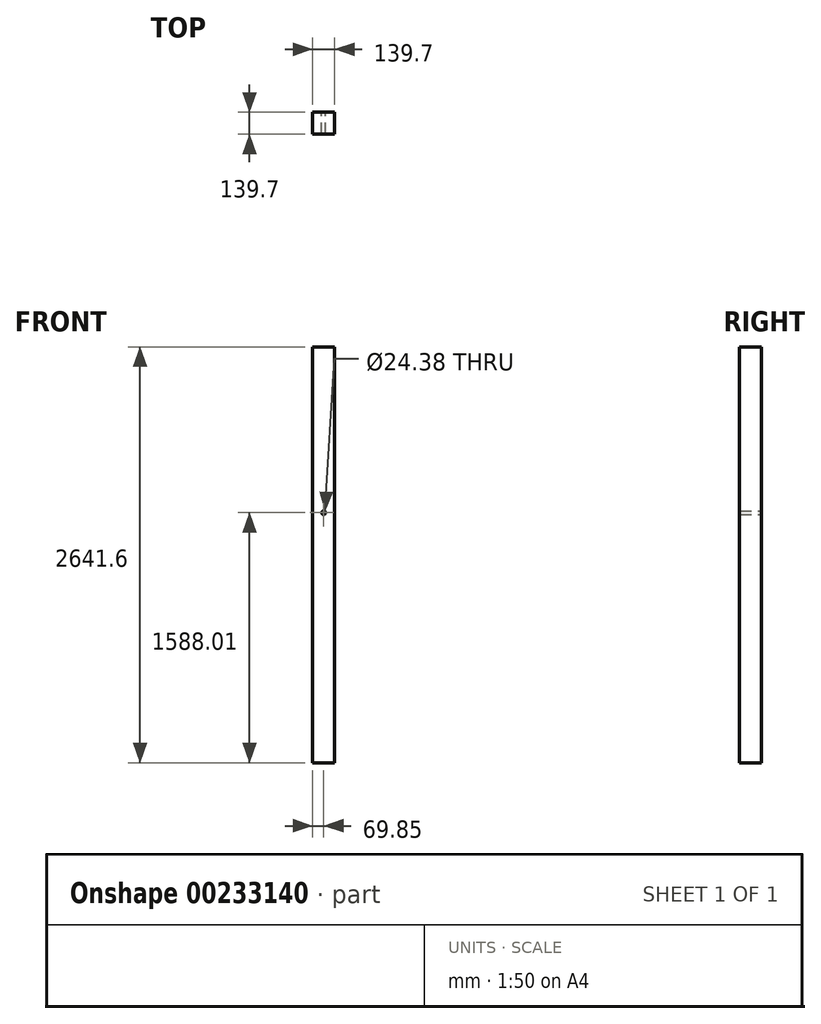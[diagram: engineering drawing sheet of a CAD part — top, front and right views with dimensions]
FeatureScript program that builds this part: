
annotation { "Feature Type Name" : "Feature", "Feature Type Description" : "" }
export const myFeature = defineFeature(function(context is Context, id is Id, definition is map)
    precondition{}
    {
        {
            var Q0;
            Q0=qCreatedBy(makeId("Front.planeOp"),FACE);
            var sketch = newSketch(context, id + "F0", { "sketchPlane" : qUnion([Q0])});
            skLineSegment(sketch, "E0.bottom", {"start": v(-69.85, 3580.95) * mm, "end": v(69.85, 3580.95) * mm});
            skLineSegment(sketch, "E0.top", {"start": v(-69.85, 939.35) * mm, "end": v(69.85, 939.35) * mm});
            skLineSegment(sketch, "E0.left", {"start": v(-69.85, 3580.95) * mm, "end": v(-69.85, 939.35) * mm});
            skLineSegment(sketch, "E0.right", {"start": v(69.85, 3580.95) * mm, "end": v(69.85, 939.35) * mm});
            skCircle(sketch, "E1", {"center": v(0, 2527.36) * mm, "radius": 12.2 * mm});
            skSolve(sketch);
        }
        {
            var Q0;
            Q0 = qSketchRegion(id + "F0", true);
            extrude(context, id + "F1", {"entities" : qUnion([Q0]), "depth" : 139.7 * mm});
        }
    });
